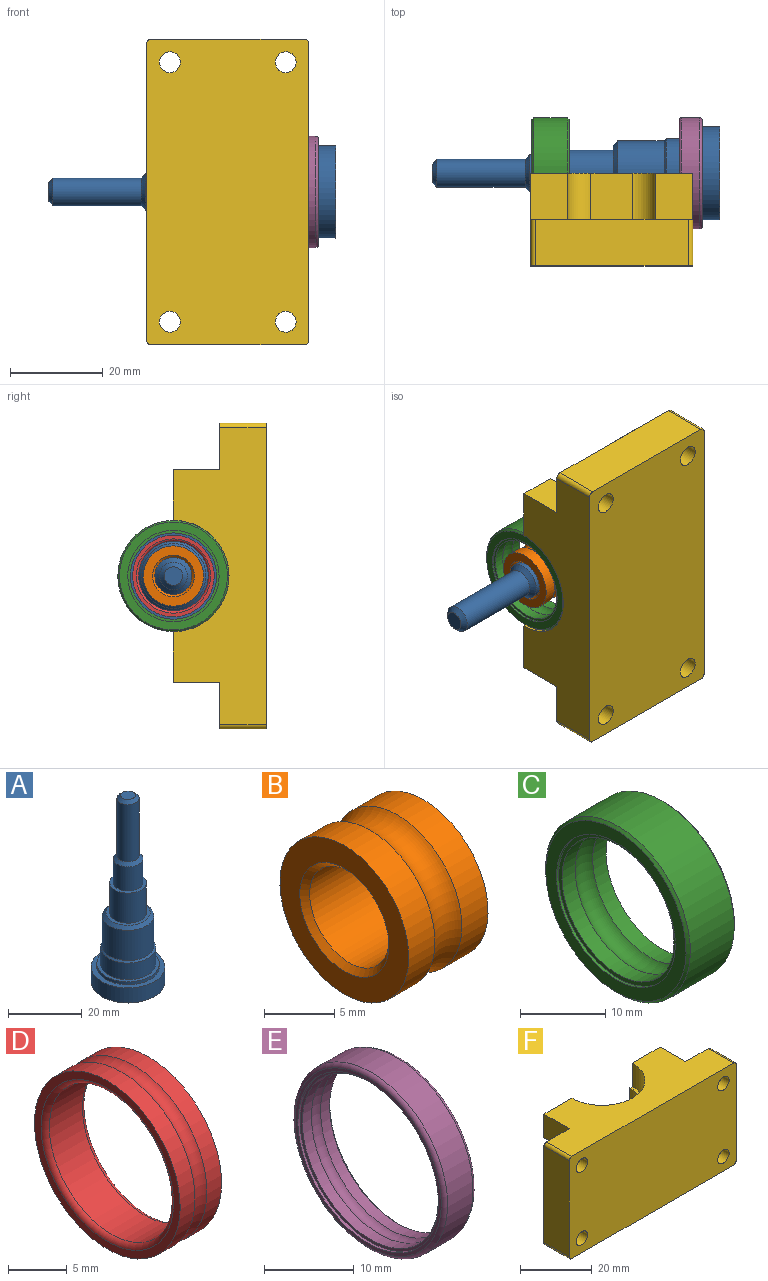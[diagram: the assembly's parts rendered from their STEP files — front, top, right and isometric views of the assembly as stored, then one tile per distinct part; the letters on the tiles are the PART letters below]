
ASSEMBLY  parts=6 mates=9
PART A: 19 faces, bbox 20x20x62 mm
  f0: plane 10x10mm, normal (0,0,1), area 28.3mm2, adj f9,f10
  f1: plane 12x12mm, normal (0,0,1), area 34.6mm2, adj f9,f14
  f2: plane 17x17mm, normal (0,0,1), area 50.3mm2, adj f6,f7
  f3: plane 20x20mm, normal (0,0,1), area 87.2mm2, adj f4,f6
  f4: cylinder r=10mm len=20mm, axis (0,0,-1), area 314.2mm2, adj f3,f5
  f5: plane 20x20mm, normal (0,0,-1), area 258.3mm2, adj f4,f16
  f6: cylinder r=8.5mm len=17mm, axis (0,0,-1), area 53.4mm2, adj f2,f3
  f7: cylinder r=7.5mm len=15mm, axis (0,0,-1), area 259.2mm2, adj f2,f18
  f8: cylinder r=7mm len=14mm, axis (0,0,-1), area 439.8mm2, adj f14,f18
  f9: cylinder r=5mm len=10mm, axis (0,0,-1), area 314.2mm2, adj f0,f1
  f10: cylinder r=4mm len=8mm, axis (0,0,-1), area 201.1mm2, adj f0,f13
  f11: cylinder r=3mm len=19mm, axis (0,0,-1), area 358.1mm2, adj f13,f17
  f12: plane 4x4mm, normal (0,0,1), area 12.6mm2, adj f17
  f13: cone r=3mm half-angle=45deg, axis (0,0,-1), area 31.1mm2, adj f10,f11
  f14: cone r=6mm half-angle=45deg, axis (0,0,-1), area 57.8mm2, adj f1,f8
  f15: cone r=4.22mm half-angle=59deg, axis (0,0,-1), area 65.2mm2, adj f16
  f16: cylinder r=4.22mm len=17mm, axis (0,0,-1), area 450.4mm2, adj f5,f15
  f17: cone r=2mm half-angle=45deg, axis (0,0,-1), area 22.2mm2, adj f11,f12
  f18: cone r=7mm half-angle=45deg, axis (0,0,-1), area 32.2mm2, adj f7,f8
PART B: 8 faces, bbox 8x14.2x14.2 mm
  f0: cylinder r=6.5mm len=13mm, axis (-1,0,0), area 108mm2, adj f1,f7
  f1: torus R=7.95mm, axis (-1,0,0), area 115.3mm2, adj f0,f2
  f2: cylinder r=6.5mm len=13mm, axis (-1,0,0), area 108mm2, adj f1,f3
  f3: plane 13x13mm, normal (1,0,0), area 69.1mm2, adj f2,f4
  f4: cone r=4mm half-angle=45deg, axis (1,0,0), area 18.9mm2, adj f3,f5
  f5: cylinder r=4mm len=8mm, axis (-1,0,0), area 175.9mm2, adj f4,f6
  f6: cone r=4.5mm half-angle=45deg, axis (-1,0,0), area 18.9mm2, adj f5,f7
  f7: plane 13x13mm, normal (-1,0,0), area 69.1mm2, adj f0,f6
PART C: 12 faces, bbox 8x24x24 mm
  f0: cone r=12mm half-angle=45deg, axis (1,0,0), area 37.1mm2, adj f1,f11
  f1: cylinder r=12mm len=24mm, axis (-1,0,0), area 549.9mm2, adj f0,f2
  f2: cone r=11.65mm half-angle=45deg, axis (-1,0,0), area 37.1mm2, adj f1,f3
  f3: plane 23.29x23.29mm, normal (1,0,0), area 121.3mm2, adj f2,f4
  f4: cylinder r=9.85mm len=19.7mm, axis (-1,0,0), area 21.7mm2, adj f3,f5
  f5: plane 19.7x19.7mm, normal (1,0,0), area 33.1mm2, adj f4,f6
  f6: cylinder r=9.3mm len=18.6mm, axis (-1,0,0), area 128.2mm2, adj f5,f7
  f7: torus R=7.95mm, axis (-1,0,0), area 199.5mm2, adj f6,f8
  f8: cylinder r=9.3mm len=18.6mm, axis (-1,0,0), area 128.2mm2, adj f7,f9
  f9: plane 19.7x19.7mm, normal (-1,0,0), area 33.1mm2, adj f8,f10
  f10: cylinder r=9.85mm len=19.7mm, axis (-1,0,0), area 21.7mm2, adj f9,f11
  f11: plane 23.29x23.29mm, normal (-1,0,0), area 121.3mm2, adj f0,f10
PART D: 8 faces, bbox 5x19.3x19.3 mm
  f0: cylinder r=8.8mm len=17.6mm, axis (-1,0,0), area 98.5mm2, adj f1,f7
  f1: plane 17.6x17.6mm, normal (-1,0,0), area 42.2mm2, adj f0,f2
  f2: torus R=8.09mm, axis (-1,0,0), area 36.6mm2, adj f1,f3
  f3: cylinder r=7.5mm len=15mm, axis (-1,0,0), area 188.5mm2, adj f2,f4
  f4: torus R=8.09mm, axis (-1,0,0), area 36.6mm2, adj f3,f5
  f5: plane 17.6x17.6mm, normal (1,0,0), area 42.2mm2, adj f4,f6
  f6: cylinder r=8.8mm len=17.6mm, axis (-1,0,0), area 98.5mm2, adj f5,f7
  f7: torus R=9.75mm, axis (-1,0,0), area 83.6mm2, adj f0,f6
PART E: 12 faces, bbox 5x26x26 mm
  f0: torus R=11.41mm, axis (-1,0,0), area 56.1mm2, adj f1,f11
  f1: plane 23x23mm, normal (-1,0,0), area 31.9mm2, adj f0,f2
  f2: cylinder r=11.05mm len=22.1mm, axis (-1,0,0), area 24.3mm2, adj f1,f3
  f3: plane 22.1x22.1mm, normal (-1,0,0), area 23.9mm2, adj f2,f4
  f4: cylinder r=10.7mm len=21.4mm, axis (-1,0,0), area 96.3mm2, adj f3,f5
  f5: torus R=9.75mm, axis (-1,0,0), area 105.1mm2, adj f4,f6
  f6: cylinder r=10.7mm len=21.4mm, axis (-1,0,0), area 96.3mm2, adj f5,f7
  f7: plane 22.1x22.1mm, normal (1,0,0), area 23.9mm2, adj f6,f8
  f8: cylinder r=11.05mm len=22.1mm, axis (-1,0,0), area 24.3mm2, adj f7,f9
  f9: plane 23x23mm, normal (1,0,0), area 31.9mm2, adj f8,f10
  f10: torus R=11.41mm, axis (-1,0,0), area 56.1mm2, adj f9,f11
  f11: cylinder r=12mm len=24mm, axis (-1,0,0), area 301.6mm2, adj f0,f10
PART F: 44 faces, bbox 66x20x35 mm
  f0: plane 66x35mm, normal (0,-1,0), area 2245.5mm2, adj f3,f4,f7,f8,f24,f25,f34,f35
  f1: plane 35x18mm, normal (0,1,0), area 459mm2, adj f2,f3,f4,f7,f16,f17,f18,f19
  f2: plane 10x9mm, normal (-1,0,0), area 90mm2, adj f1,f5,f42,f43
  f3: plane 64x20mm, normal (0,0,1), area 873.8mm2, adj f0,f1,f5,f6,f9,f11,f17,f27
  f4: plane 64x20mm, normal (0,0,-1), area 873.8mm2, adj f0,f1,f5,f6,f9,f15,f19,f29
  f5: plane 35x12mm, normal (0,1,0), area 255.9mm2, adj f2,f3,f4,f11,f12,f13,f14,f15
  f6: plane 35x12mm, normal (0,1,0), area 255.9mm2, adj f3,f4,f10,f11,f12,f13,f14,f15
  f7: plane 33x10mm, normal (-1,0,0), area 330mm2, adj f0,f1,f36,f39
  f8: plane 33x10mm, normal (1,0,0), area 330mm2, adj f0,f9,f37,f38
  f9: plane 35x18mm, normal (0,1,0), area 459mm2, adj f3,f4,f8,f10,f26,f27,f28,f29
  f10: plane 10x9mm, normal (1,0,0), area 90mm2, adj f6,f9,f40,f41
  f11: cylinder r=12mm len=24mm, axis (0,0,1), area 301.6mm2, adj f3,f5,f6,f12
  f12: plane 24x12mm, normal (0,0,1), area 36.1mm2, adj f5,f6,f11,f13
  f13: cylinder r=11mm len=22mm, axis (0,0,1), area 760.3mm2, adj f5,f6,f12,f14
  f14: plane 24x12mm, normal (0,0,-1), area 36.1mm2, adj f5,f6,f13,f15
  f15: cylinder r=12mm len=24mm, axis (0,0,1), area 188.5mm2, adj f4,f5,f6,f14
  f16: plane 10x3mm, normal (0,0,-1), area 30mm2, adj f1,f5,f17,f42
  f17: plane 10x8mm, normal (-1,0,0), area 80mm2, adj f1,f3,f5,f16
  f18: plane 10x3mm, normal (0,0,1), area 30mm2, adj f1,f5,f19,f43
  f19: plane 10x8mm, normal (-1,0,0), area 80mm2, adj f1,f4,f5,f18
  f20: cone r=1.25mm half-angle=59deg, axis (0,1,0), area 5.7mm2, adj f21
  f21: cylinder r=1.25mm len=8mm, axis (0,1,0), area 62.8mm2, adj f5,f20
  f22: cone r=1.25mm half-angle=59deg, axis (0,1,0), area 5.7mm2, adj f23
  f23: cylinder r=1.25mm len=8mm, axis (0,1,0), area 62.8mm2, adj f5,f22
  f24: cylinder r=2.25mm len=10mm, axis (0,1,0), area 141.4mm2, adj f0,f1
  f25: cylinder r=2.25mm len=10mm, axis (0,1,0), area 141.4mm2, adj f0,f1
  f26: plane 10x3mm, normal (0,0,-1), area 30mm2, adj f6,f9,f27,f40
  f27: plane 10x8mm, normal (1,0,0), area 80mm2, adj f3,f6,f9,f26
  f28: plane 10x3mm, normal (0,0,1), area 30mm2, adj f6,f9,f29,f41
  f29: plane 10x8mm, normal (1,0,0), area 80mm2, adj f4,f6,f9,f28
  f30: cone r=1.25mm half-angle=59deg, axis (0,1,0), area 5.7mm2, adj f31
  f31: cylinder r=1.25mm len=8mm, axis (0,1,0), area 62.8mm2, adj f6,f30
  f32: cone r=1.25mm half-angle=59deg, axis (0,1,0), area 5.7mm2, adj f33
  f33: cylinder r=1.25mm len=8mm, axis (0,1,0), area 62.8mm2, adj f6,f32
  f34: cylinder r=2.25mm len=10mm, axis (0,1,0), area 141.4mm2, adj f0,f9
  f35: cylinder r=2.25mm len=10mm, axis (0,1,0), area 141.4mm2, adj f0,f9
  f36: cylinder r=1mm len=10mm, axis (0,-1,0), area 15.7mm2, adj f0,f1,f4,f7
  f37: cylinder r=1mm len=10mm, axis (0,-1,0), area 15.7mm2, adj f0,f4,f8,f9
  f38: cylinder r=1mm len=10mm, axis (0,-1,0), area 15.7mm2, adj f0,f3,f8,f9
  f39: cylinder r=1mm len=10mm, axis (0,-1,0), area 15.7mm2, adj f0,f1,f3,f7
  f40: cylinder r=5mm len=10mm, axis (0,-1,0), area 78.5mm2, adj f6,f9,f10,f26
  f41: cylinder r=5mm len=10mm, axis (0,1,0), area 78.5mm2, adj f6,f9,f10,f28
  f42: cylinder r=5mm len=10mm, axis (0,1,0), area 78.5mm2, adj f1,f2,f5,f16
  f43: cylinder r=5mm len=10mm, axis (0,-1,0), area 78.5mm2, adj f1,f2,f5,f18
PLACE A rot(axis=(0,-1,0),90deg) t=(6.12,-38.46,-21.37)mm
PLACE B t=(-34.38,-38.46,-21.37)mm
PLACE C t=(-34.38,-38.46,-21.37)mm
PLACE D t=(-2.63,-38.46,-21.37)mm
PLACE E t=(-2.63,-38.46,-21.37)mm
PLACE F rot(axis=(0,-1,0),90deg) t=(-17.16,-58.46,-21.37)mm
MATE cylindrical A.f4 <-> D.f0  axis (-1,0,0) through (-54.88,-38.46,-21.37)mm
MATE cylindrical C.f0 <-> B.f0  axis (-1,0,0) through (-28.92,-38.46,-21.37)mm
MATE cylindrical F.f11 <-> A.f4  axis (1,0,0) through (-4.66,-38.46,-21.37)mm
MATE fastened A.f4 <-> B.f0  axis (1,0,0) through (-26.88,-38.46,-21.37)mm
MATE cylindrical E.f0 <-> D.f0  axis (-1,0,0) through (-0.85,-38.46,-21.37)mm
MATE planar C.f0 <-> B.f0  axis (1,0,0) through (-26.38,-38.46,-21.37)mm
MATE planar E.f0 <-> D.f0  axis (1,0,0) through (2.37,-38.46,-21.37)mm
MATE cylindrical A.f4 <-> C.f0  axis (1,0,0) through (6.12,-38.46,-21.37)mm
MATE fastened A.f4 <-> D.f0  axis (1,0,0) through (-2.63,-38.46,-21.37)mm
